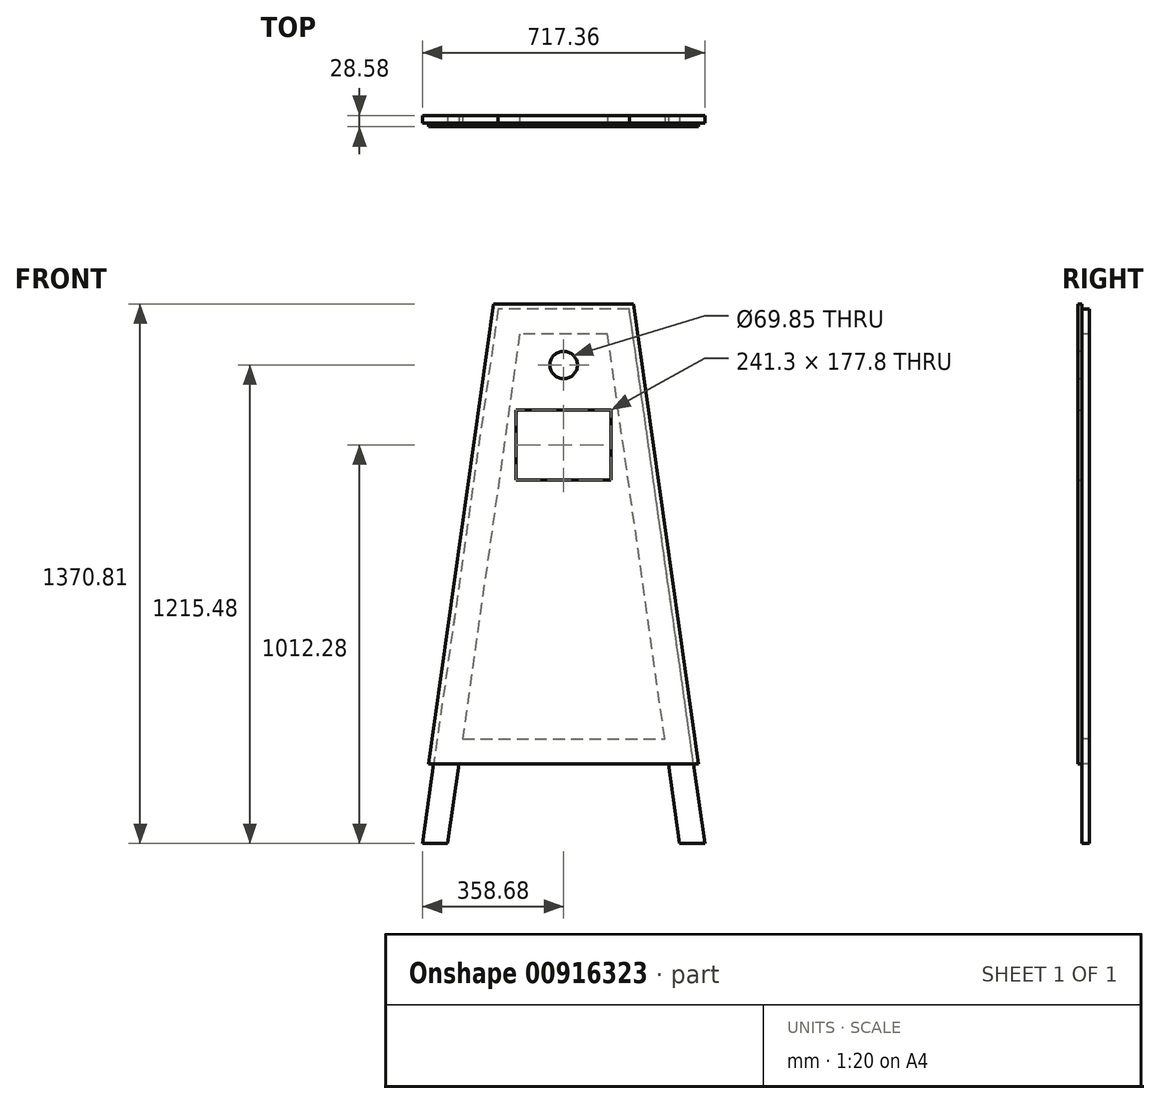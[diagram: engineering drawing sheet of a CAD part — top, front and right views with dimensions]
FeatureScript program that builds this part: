
annotation { "Feature Type Name" : "Feature", "Feature Type Description" : "" }
export const myFeature = defineFeature(function(context is Context, id is Id, definition is map)
    precondition{}
    {
        {
            var Q0;
            Q0=qCreatedBy(makeId("Front.planeOp"),FACE);
            var sketch = newSketch(context, id + "F0", { "sketchPlane" : qUnion([Q0])});
            skLineSegment(sketch, "E0", {"start": v(-342.9, 0) * mm, "end": v(-177.8, 1168.4) * mm});
            skLineSegment(sketch, "E1", {"start": v(-177.8, 1168.4) * mm, "end": v(177.8, 1168.4) * mm});
            skLineSegment(sketch, "E2", {"start": v(177.8, 1168.4) * mm, "end": v(342.9, 0) * mm});
            skLineSegment(sketch, "E3", {"start": v(342.9, 0) * mm, "end": v(-342.9, 0) * mm});
            skPoint(sketch, "E4", {"position": v(0, 0) * mm});
            skPoint(sketch, "E5", {"position": v(0, 1168.4) * mm});
            skPoint(sketch, "E6", {"position": v(-215.9, 898.77) * mm});
            skPoint(sketch, "E7", {"position": v(215.9, 898.77) * mm});
            skLineSegment(sketch, "E8", {"start": v(120.65, 898.77) * mm, "end": v(120.65, 720.97) * mm});
            skLineSegment(sketch, "E9", {"start": v(120.65, 720.97) * mm, "end": v(-120.65, 720.97) * mm});
            skLineSegment(sketch, "E10", {"start": v(-120.65, 720.97) * mm, "end": v(-120.65, 898.77) * mm});
            skPoint(sketch, "E11", {"position": v(0, 720.97) * mm});
            skLineSegment(sketch, "E12", {"start": v(120.65, 898.77) * mm, "end": v(-120.65, 898.77) * mm});
            skPoint(sketch, "E13", {"position": v(0, 898.77) * mm});
            skCircle(sketch, "E14", {"center": v(0, 1013.07) * mm, "radius": 34.93 * mm});
            skSolve(sketch);
        }
        {
            var Q0;
            Q0 = qSketchRegion(id + "F0", true);
            extrude(context, id + "F1", {"entities" : qUnion([Q0]), "depth" : 9.52 * mm, "offsetDistance" : 25.4 * mm});
        }
        {
            var Q0;
            Q0=makeQuery(id+"F1.opExtrude","CAP_FACE",FACE,{"disambiguationData":[OSD([sQuery(id+"F0.wireOp",EDGE,"E0"),sQuery(id+"F0.wireOp",EDGE,"E1"),sQuery(id+"F0.wireOp",EDGE,"E2"),sQuery(id+"F0.wireOp",EDGE,"E3")])],"isStart":true});
            var sketch = newSketch(context, id + "F2", { "sketchPlane" : qUnion([Q0])});
            skLineSegment(sketch, "E15", {"start": v(-358.68, -202.4) * mm, "end": v(-166.77, 1155.7) * mm});
            skLineSegment(sketch, "E16", {"start": v(-166.77, 1155.7) * mm, "end": v(166.77, 1155.7) * mm});
            skLineSegment(sketch, "E17", {"start": v(166.77, 1155.7) * mm, "end": v(358.68, -202.4) * mm});
            skPoint(sketch, "E18", {"position": v(0, 1168.4) * mm});
            skPoint(sketch, "E19", {"position": v(0, 1155.7) * mm});
            skPoint(sketch, "E20", {"position": v(0, 9.53) * mm});
            skLineSegment(sketch, "E21", {"start": v(-256.97, 63.5) * mm, "end": v(-111.61, 1092.2) * mm});
            skLineSegment(sketch, "E22", {"start": v(-111.61, 1092.2) * mm, "end": v(111.61, 1092.2) * mm});
            skLineSegment(sketch, "E23", {"start": v(111.61, 1092.2) * mm, "end": v(256.97, 63.5) * mm});
            skLineSegment(sketch, "E24", {"start": v(256.97, 63.5) * mm, "end": v(-256.97, 63.5) * mm});
            skPoint(sketch, "E25", {"position": v(0, 1092.2) * mm});
            skPoint(sketch, "E26", {"position": v(0, 63.5) * mm});
            skLineSegment(sketch, "E27", {"start": v(-358.68, -202.4) * mm, "end": v(-294.54, -202.4) * mm});
            skLineSegment(sketch, "E28", {"start": v(-294.54, -202.4) * mm, "end": v(-265.94, 0) * mm});
            skLineSegment(sketch, "E29", {"start": v(-265.94, 0) * mm, "end": v(265.94, 0) * mm});
            skLineSegment(sketch, "E30", {"start": v(265.94, 0) * mm, "end": v(294.54, -202.4) * mm});
            skLineSegment(sketch, "E31", {"start": v(294.54, -202.4) * mm, "end": v(358.68, -202.4) * mm});
            skLineSegment(sketch, "E32", {"start": v(166.77, 1155.7) * mm, "end": v(111.61, 1092.2) * mm});
            skLineSegment(sketch, "E33", {"start": v(-166.77, 1155.7) * mm, "end": v(-111.61, 1092.2) * mm});
            skSolve(sketch);
        }
        {
            var Q0;
            Q0 = qSketchRegion(id + "F2", true);
            extrude(context, id + "F3", {"entities" : qUnion([Q0]), "operationType" : NewBodyOperationType.ADD, "depth" : 19.05 * mm, "offsetDistance" : 25.4 * mm});
        }
    });
